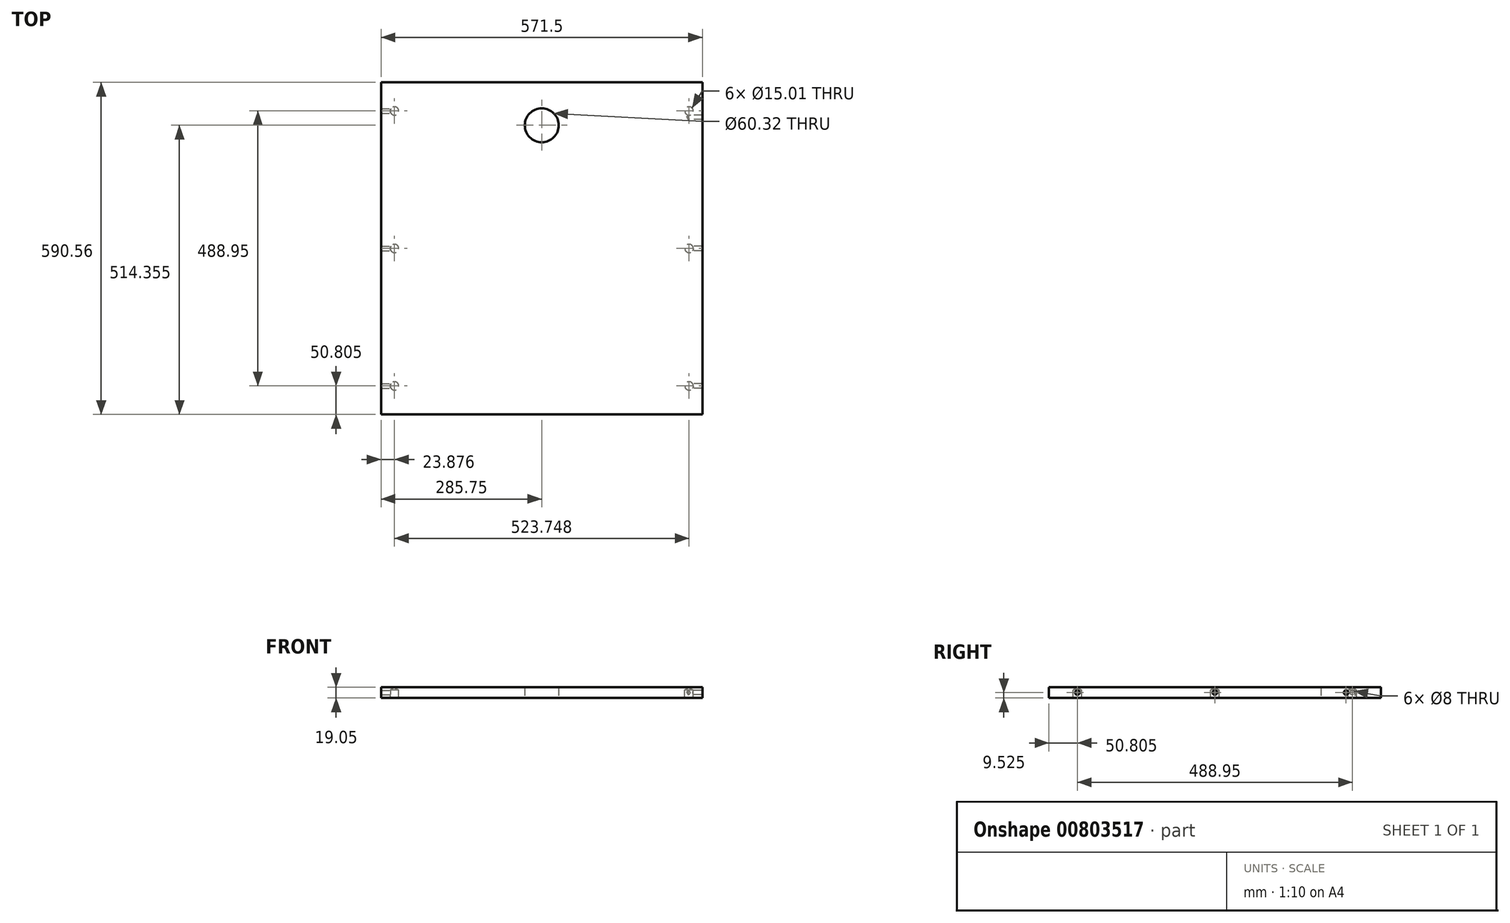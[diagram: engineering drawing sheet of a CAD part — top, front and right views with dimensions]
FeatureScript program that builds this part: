
annotation { "Feature Type Name" : "Feature", "Feature Type Description" : "" }
export const myFeature = defineFeature(function(context is Context, id is Id, definition is map)
    precondition{}
    {
        {
            var Q0;
            Q0=qCreatedBy(makeId("Top.planeOp"),FACE);
            var sketch = newSketch(context, id + "F0", { "sketchPlane" : qUnion([Q0])});
            skLineSegment(sketch, "E0.bottom", {"start": v(285.75, 295.28) * mm, "end": v(-285.75, 295.28) * mm});
            skLineSegment(sketch, "E0.top", {"start": v(285.75, -295.27) * mm, "end": v(-285.75, -295.28) * mm});
            skLineSegment(sketch, "E0.left", {"start": v(285.75, 295.28) * mm, "end": v(285.75, -295.27) * mm});
            skLineSegment(sketch, "E0.right", {"start": v(-285.75, 295.28) * mm, "end": v(-285.75, -295.28) * mm});
            skPoint(sketch, "E0.middle", {"position": v(0, 0) * mm});
            skLineSegment(sketch, "E1", {"start": v(0, 295.28) * mm, "end": v(0, 219.08) * mm});
            skCircle(sketch, "E2", {"center": v(0, 219.08) * mm, "radius": 30.16 * mm});
            skSolve(sketch);
        }
        {
            var Q0;
            Q0=makeQuery(id+"F0.imprint","IMPRINT",FACE,{"disambiguationData":[TD([[makeQuery(id+"F0.imprint","IMPRINT",EDGE,{"derivedFrom":sQuery(id+"F0.wireOp",EDGE,"E0.top")}),-1.0]])]});
            extrude(context, id + "F1", {"entities" : qUnion([Q0]), "depth" : 19.05 * mm, "offsetDistance" : 25.4 * mm});
        }
        {
            var Q0;
            Q0=makeQuery(id+"F1.opExtrude","CAP_FACE",FACE,{"disambiguationData":[OSD([sQuery(id+"F0.wireOp",EDGE,"E0.bottom"),sQuery(id+"F0.wireOp",EDGE,"E0.top"),sQuery(id+"F0.wireOp",EDGE,"E0.left"),sQuery(id+"F0.wireOp",EDGE,"E0.right"),sQuery(id+"F0.wireOp",EDGE,"E2")])],"isStart":true});
            var sketch = newSketch(context, id + "F2", { "sketchPlane" : qUnion([Q0])});
            skLineSegment(sketch, "E3", {"start": v(-285.75, 295.28) * mm, "end": v(-261.87, 295.28) * mm});
            skLineSegment(sketch, "E4", {"start": v(-261.87, 295.28) * mm, "end": v(-261.87, 244.48) * mm});
            skLineSegment(sketch, "E5", {"start": v(-285.75, -295.27) * mm, "end": v(-261.87, -295.27) * mm});
            skLineSegment(sketch, "E6", {"start": v(-261.87, -295.27) * mm, "end": v(-261.87, -244.47) * mm});
            skLineSegment(sketch, "E7", {"start": v(-285.75, 0) * mm, "end": v(-261.87, 0) * mm});
            skLineSegment(sketch, "E8", {"start": v(285.75, 0) * mm, "end": v(261.87, 0) * mm});
            skLineSegment(sketch, "E9", {"start": v(285.75, 295.28) * mm, "end": v(261.87, 295.28) * mm});
            skLineSegment(sketch, "E10", {"start": v(261.87, 295.28) * mm, "end": v(261.87, 244.48) * mm});
            skLineSegment(sketch, "E11", {"start": v(285.75, -295.27) * mm, "end": v(261.87, -295.27) * mm});
            skLineSegment(sketch, "E12", {"start": v(261.87, -295.27) * mm, "end": v(261.87, -244.47) * mm});
            skPoint(sketch, "E13", {"position": v(-261.87, 244.48) * mm});
            skPoint(sketch, "E14", {"position": v(-261.87, 0) * mm});
            skPoint(sketch, "E15", {"position": v(-261.87, -244.47) * mm});
            skPoint(sketch, "E16", {"position": v(261.87, -244.47) * mm});
            skPoint(sketch, "E17", {"position": v(261.87, 0) * mm});
            skPoint(sketch, "E18", {"position": v(261.87, 244.48) * mm});
            skSolve(sketch);
        }
        {
            var Q0;
            Q0=sQuery(id+"F2.wireOp",VERTEX,"E13");
            var Q1;
            Q1=sQuery(id+"F2.wireOp",VERTEX,"E18");
            var Q2;
            Q2=sQuery(id+"F2.wireOp",VERTEX,"E14");
            var Q3;
            Q3=sQuery(id+"F2.wireOp",VERTEX,"E17");
            var Q4;
            Q4=sQuery(id+"F2.wireOp",VERTEX,"E16");
            var Q5;
            Q5=sQuery(id+"F2.wireOp",VERTEX,"E15");
            var Q6;
            Q6=makeQuery(id+"F1.opExtrude","SWEPT_BODY",BODY,{"disambiguationData":[OSD([sQuery(id+"F0.wireOp",EDGE,"E0.bottom"),sQuery(id+"F0.wireOp",EDGE,"E0.top"),sQuery(id+"F0.wireOp",EDGE,"E0.left"),sQuery(id+"F0.wireOp",EDGE,"E0.right"),sQuery(id+"F0.wireOp",EDGE,"E2")])]});
            hole(context, id + "F3", {"style" : HoleStyle.SIMPLE, "endStyle" : HoleEndStyle.BLIND, "holeDiameter" : 15 * mm, "majorDiameter" : 6.35 * mm, "holeDepth" : 14.22 * mm, "isTappedThrough" : true, "tappedDepth" : 12.7 * mm, "tapClearance" : 3, "startFromSketch" : true, "locations" : qUnion([Q0, Q1, Q2, Q3, Q4, Q5]), "scope" : qUnion([Q6])});
        }
        {
            var Q0;
            Q0=makeQuery(id+"F1.opExtrude","SWEPT_FACE",FACE,{"disambiguationData":[OSD([sQuery(id+"F0.wireOp",EDGE,"E0.left")])]});
            var sketch = newSketch(context, id + "F4", { "sketchPlane" : qUnion([Q0])});
            skPoint(sketch, "E19", {"position": v(0, 9.52) * mm});
            skPoint(sketch, "E19.positionSnap0", {"position": v(0, 19.05) * mm});
            skPoint(sketch, "E20", {"position": v(-244.47, 9.52) * mm});
            skPoint(sketch, "E21", {"position": v(233.36, 9.52) * mm});
            skLineSegment(sketch, "E22", {"start": v(-244.47, 9.52) * mm, "end": v(-244.47, 0) * mm});
            skLineSegment(sketch, "E23", {"start": v(-244.47, 0) * mm, "end": v(-295.27, 0) * mm});
            skLineSegment(sketch, "E24", {"start": v(0, 0) * mm, "end": v(0, 9.53) * mm});
            skPoint(sketch, "E25", {"position": v(0, 9.53) * mm});
            skLineSegment(sketch, "E26", {"start": v(233.36, 9.52) * mm, "end": v(233.36, 0) * mm});
            skSolve(sketch);
        }
        {
            var Q0;
            Q0=sQuery(id+"F4.wireOp",VERTEX,"E20");
            var Q1;
            Q1=sQuery(id+"F4.wireOp",VERTEX,"E19");
            var Q2;
            Q2=sQuery(id+"F4.wireOp",VERTEX,"E21");
            var Q3;
            Q3=makeQuery(id+"F1.opExtrude","SWEPT_BODY",BODY,{"disambiguationData":[OSD([sQuery(id+"F0.wireOp",EDGE,"E0.bottom"),sQuery(id+"F0.wireOp",EDGE,"E0.top"),sQuery(id+"F0.wireOp",EDGE,"E0.left"),sQuery(id+"F0.wireOp",EDGE,"E0.right"),sQuery(id+"F0.wireOp",EDGE,"E2")])]});
            hole(context, id + "F5", {"style" : HoleStyle.SIMPLE, "endStyle" : HoleEndStyle.BLIND, "holeDiameter" : 8 * mm, "majorDiameter" : 6.35 * mm, "holeDepth" : 25.4 * mm, "isTappedThrough" : true, "tappedDepth" : 12.7 * mm, "tapClearance" : 3, "startFromSketch" : true, "locations" : qUnion([Q0, Q1, Q2]), "scope" : qUnion([Q3])});
        }
        {
            var Q0;
            Q0=makeQuery(id+"F1.opExtrude","SWEPT_FACE",FACE,{"disambiguationData":[OSD([sQuery(id+"F0.wireOp",EDGE,"E0.right")])]});
            var sketch = newSketch(context, id + "F6", { "sketchPlane" : qUnion([Q0])});
            skPoint(sketch, "E27", {"position": v(-244.47, 9.52) * mm});
            skPoint(sketch, "E28", {"position": v(244.47, 9.53) * mm});
            skLineSegment(sketch, "E29", {"start": v(0, 0) * mm, "end": v(0, 9.53) * mm});
            skPoint(sketch, "E30", {"position": v(0, 9.53) * mm});
            skLineSegment(sketch, "E31", {"start": v(-244.47, 9.52) * mm, "end": v(-244.47, 0) * mm});
            skLineSegment(sketch, "E32", {"start": v(-244.47, 0) * mm, "end": v(-295.28, 0) * mm});
            skLineSegment(sketch, "E33", {"start": v(244.47, 9.53) * mm, "end": v(244.47, 0) * mm});
            skLineSegment(sketch, "E34", {"start": v(244.47, 0) * mm, "end": v(295.28, 0) * mm});
            skSolve(sketch);
        }
        {
            var Q0;
            Q0=sQuery(id+"F6.wireOp",VERTEX,"7JFDCdo1-Y3dr-wsHc-LP2G-7qkS5dpKQL4z.end");
            var Q1;
            Q1=sQuery(id+"F6.wireOp",VERTEX,"E30");
            var Q2;
            Q2=sQuery(id+"F6.wireOp",VERTEX,"E28");
            var Q3;
            Q3=sQuery(id+"F6.wireOp",VERTEX,"E27");
            var Q4;
            Q4=makeQuery(id+"F1.opExtrude","SWEPT_BODY",BODY,{"disambiguationData":[OSD([sQuery(id+"F0.wireOp",EDGE,"E0.bottom"),sQuery(id+"F0.wireOp",EDGE,"E0.top"),sQuery(id+"F0.wireOp",EDGE,"E0.left"),sQuery(id+"F0.wireOp",EDGE,"E0.right"),sQuery(id+"F0.wireOp",EDGE,"E2")])]});
            hole(context, id + "F7", {"style" : HoleStyle.SIMPLE, "endStyle" : HoleEndStyle.BLIND, "holeDiameter" : 8 * mm, "majorDiameter" : 6.35 * mm, "holeDepth" : 25.4 * mm, "isTappedThrough" : true, "tappedDepth" : 12.7 * mm, "tapClearance" : 3, "startFromSketch" : true, "locations" : qUnion([Q0, Q1, Q2, Q3]), "scope" : qUnion([Q4])});
        }
    });
